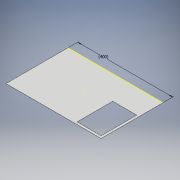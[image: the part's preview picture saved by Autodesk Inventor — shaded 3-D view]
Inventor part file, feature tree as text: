
AUTODESK INVENTOR PART (.ipt)
format: ipt  version: 2017 (Build 210142000, 142)  size: 113,152 bytes
history: native  units: mm
features: sketch x4, other x2, sheet_metal_op x1
ambient origin geometry x8: Origin, YZ Plane, XZ Plane, XY Plane, X Axis, Y Axis, Z Axis, Center Point
bodies: Solid1 (feature_tree)
feature tree (7):
  sheet_metal_op  "Face1"
  sketch  "Sketch3"  dims[d2=0.5mm]
  sketch  "Sketch4"  dims[d3=380.0mm d4=240.0mm d5=244.0mm d6=244.0mm d7=101.0mm d8=150.0mm d9=0.5mm d10=0.0mm d11=400.0mm]
  sketch  "Sketch1"  dims[d0=400.0mm]
  other  "Plate1"
  sketch  "Sketch2"  dims[d1=260.0mm]
  other  "Cut1"
